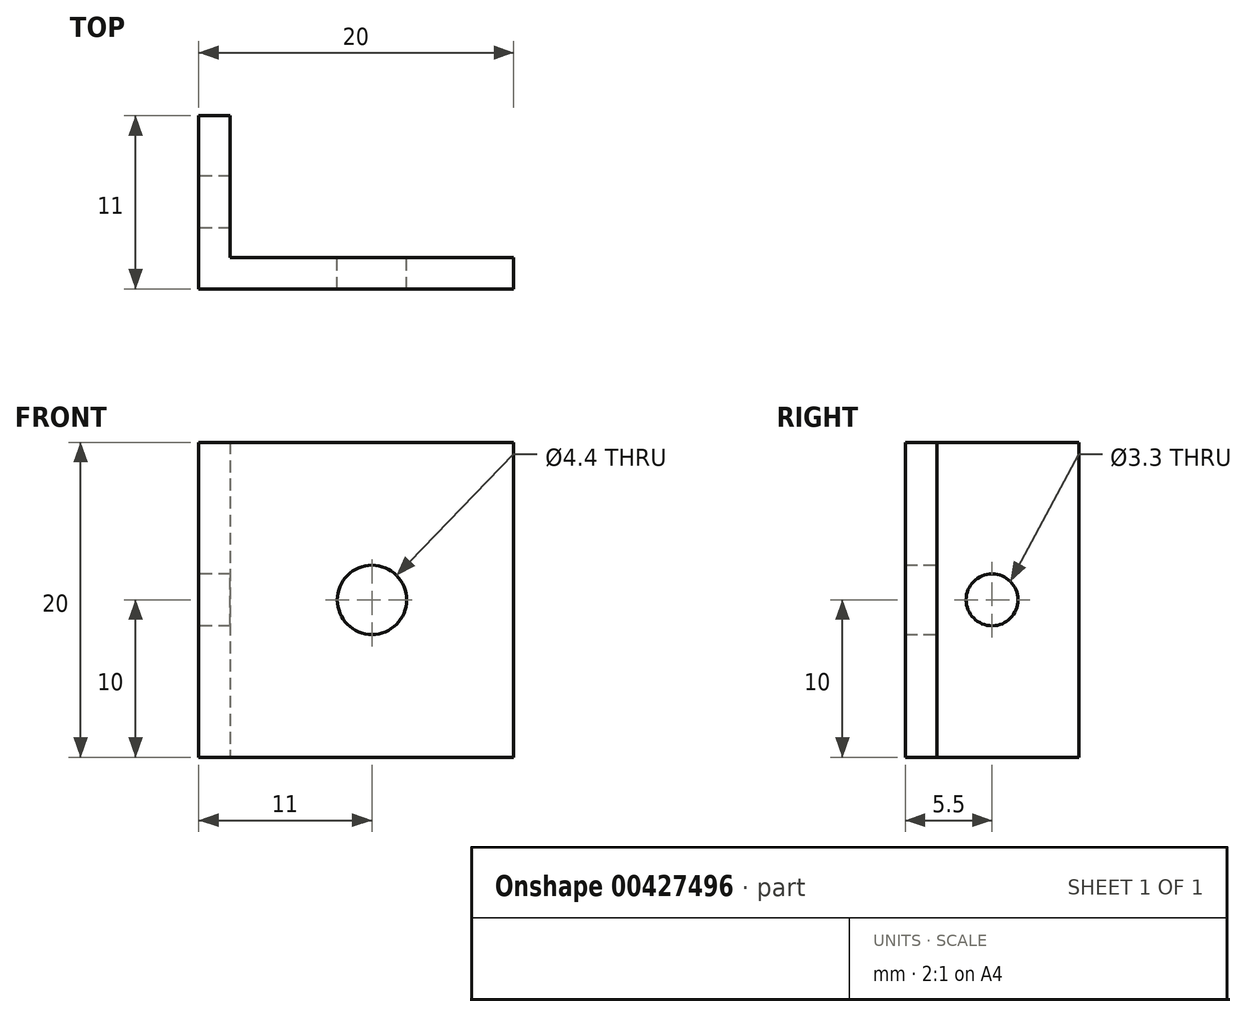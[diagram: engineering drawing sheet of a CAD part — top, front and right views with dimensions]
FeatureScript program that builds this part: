
annotation { "Feature Type Name" : "Feature", "Feature Type Description" : "" }
export const myFeature = defineFeature(function(context is Context, id is Id, definition is map)
    precondition{}
    {
        {
            var Q0;
            Q0=qCreatedBy(makeId("Top.planeOp"),FACE);
            var sketch = newSketch(context, id + "F0", { "sketchPlane" : qUnion([Q0])});
            skLineSegment(sketch, "E0", {"start": v(0, 0) * mm, "end": v(0, 11) * mm});
            skLineSegment(sketch, "E1", {"start": v(0, 11) * mm, "end": v(2, 11) * mm});
            skLineSegment(sketch, "E2", {"start": v(2, 11) * mm, "end": v(2, 2) * mm});
            skLineSegment(sketch, "E3", {"start": v(2, 2) * mm, "end": v(20, 2) * mm});
            skLineSegment(sketch, "E4", {"start": v(20, 2) * mm, "end": v(20, 0) * mm});
            skLineSegment(sketch, "E5", {"start": v(20, 0) * mm, "end": v(0, 0) * mm});
            skSolve(sketch);
        }
        {
            var Q0;
            Q0=makeQuery(id+"F0.imprint","IMPRINT",FACE,{"disambiguationData":[TD([[makeQuery(id+"F0.imprint","IMPRINT",EDGE,{"derivedFrom":sQuery(id+"F0.wireOp",EDGE,"E0")}),-1.0]])]});
            extrude(context, id + "F1", {"entities" : qUnion([Q0]), "depth" : 20 * mm});
        }
        {
            var Q0;
            Q0=makeQuery(id+"F1.opExtrude","SWEPT_FACE",FACE,{"disambiguationData":[OSD([sQuery(id+"F0.wireOp",EDGE,"E3")])]});
            var sketch = newSketch(context, id + "F2", { "sketchPlane" : qUnion([Q0])});
            skLineSegment(sketch, "E6.bottom", {"start": v(-2, 0) * mm, "end": v(-20, 0) * mm});
            skLineSegment(sketch, "E6.top", {"start": v(-2, 20) * mm, "end": v(-20, 20) * mm});
            skLineSegment(sketch, "E6.left", {"start": v(-2, 0) * mm, "end": v(-2, 20) * mm});
            skLineSegment(sketch, "E6.right", {"start": v(-20, 0) * mm, "end": v(-20, 20) * mm});
            skCircle(sketch, "E7", {"center": v(-11, 10) * mm, "radius": 6.21 * mm});
            skPoint(sketch, "E7.centerSnap0", {"position": v(-2, 10) * mm});
            skPoint(sketch, "E7.centerSnap1", {"position": v(-11, 0) * mm});
            skSolve(sketch);
        }
        {
            var Q0;
            Q0=sQuery(id+"F2.wireOp",VERTEX,"E7.center");
            var Q1;
            Q1=makeQuery(id+"F1.opExtrude","SWEPT_BODY",BODY,{"disambiguationData":[OSD([sQuery(id+"F0.wireOp",EDGE,"E0"),sQuery(id+"F0.wireOp",EDGE,"E1"),sQuery(id+"F0.wireOp",EDGE,"E2"),sQuery(id+"F0.wireOp",EDGE,"E3"),sQuery(id+"F0.wireOp",EDGE,"E4"),sQuery(id+"F0.wireOp",EDGE,"E5")])]});
            hole(context, id + "F3", {"style" : HoleStyle.SIMPLE, "endStyle" : HoleEndStyle.THROUGH, "standardTappedOrClearance" : lookupTablePath({ "standard" : "ISO", "fit" : "Normal", "size" : "M4", "type" : "Clearance" }), "standardBlindInLast" : lookupTablePath({ "fit" : "Standard", "standard" : "ISO", "size" : "M4", "type" : "Clearance" }), "holeDiameter" : 4.4 * mm, "isTappedThrough" : true, "tappedDepth" : 12 * mm, "tapClearance" : 3, "locations" : qUnion([Q0]), "scope" : qUnion([Q1])});
        }
        {
            var Q0;
            Q0=makeQuery(id+"F1.opExtrude","SWEPT_FACE",FACE,{"disambiguationData":[OSD([sQuery(id+"F0.wireOp",EDGE,"E0")])]});
            var sketch = newSketch(context, id + "F4", { "sketchPlane" : qUnion([Q0])});
            skLineSegment(sketch, "E8.bottom", {"start": v(0, 0) * mm, "end": v(-11, 0) * mm});
            skLineSegment(sketch, "E8.top", {"start": v(0, 20) * mm, "end": v(-11, 20) * mm});
            skLineSegment(sketch, "E8.left", {"start": v(0, 0) * mm, "end": v(0, 20) * mm});
            skLineSegment(sketch, "E8.right", {"start": v(-11, 0) * mm, "end": v(-11, 20) * mm});
            skCircle(sketch, "E9", {"center": v(-5.5, 10) * mm, "radius": 3.59 * mm});
            skPoint(sketch, "E9.centerSnap0", {"position": v(0, 10) * mm});
            skPoint(sketch, "E9.centerSnap1", {"position": v(-5.5, 0) * mm});
            skSolve(sketch);
        }
        {
            var Q0;
            Q0=sQuery(id+"F4.wireOp",VERTEX,"E9.center");
            var Q1;
            Q1=makeQuery(id+"F1.opExtrude","SWEPT_BODY",BODY,{"disambiguationData":[OSD([sQuery(id+"F0.wireOp",EDGE,"E0"),sQuery(id+"F0.wireOp",EDGE,"E1"),sQuery(id+"F0.wireOp",EDGE,"E2"),sQuery(id+"F0.wireOp",EDGE,"E3"),sQuery(id+"F0.wireOp",EDGE,"E4"),sQuery(id+"F0.wireOp",EDGE,"E5")])]});
            hole(context, id + "F5", {"style" : HoleStyle.SIMPLE, "endStyle" : HoleEndStyle.THROUGH, "standardTappedOrClearance" : lookupTablePath({ "standard" : "ISO", "fit" : "Normal", "size" : "M3", "type" : "Clearance" }), "standardBlindInLast" : lookupTablePath({ "fit" : "Standard", "standard" : "ISO", "size" : "M3", "type" : "Clearance" }), "holeDiameter" : 3.3 * mm, "isTappedThrough" : true, "tappedDepth" : 12 * mm, "tapClearance" : 3, "locations" : qUnion([Q0]), "scope" : qUnion([Q1])});
        }
    });
